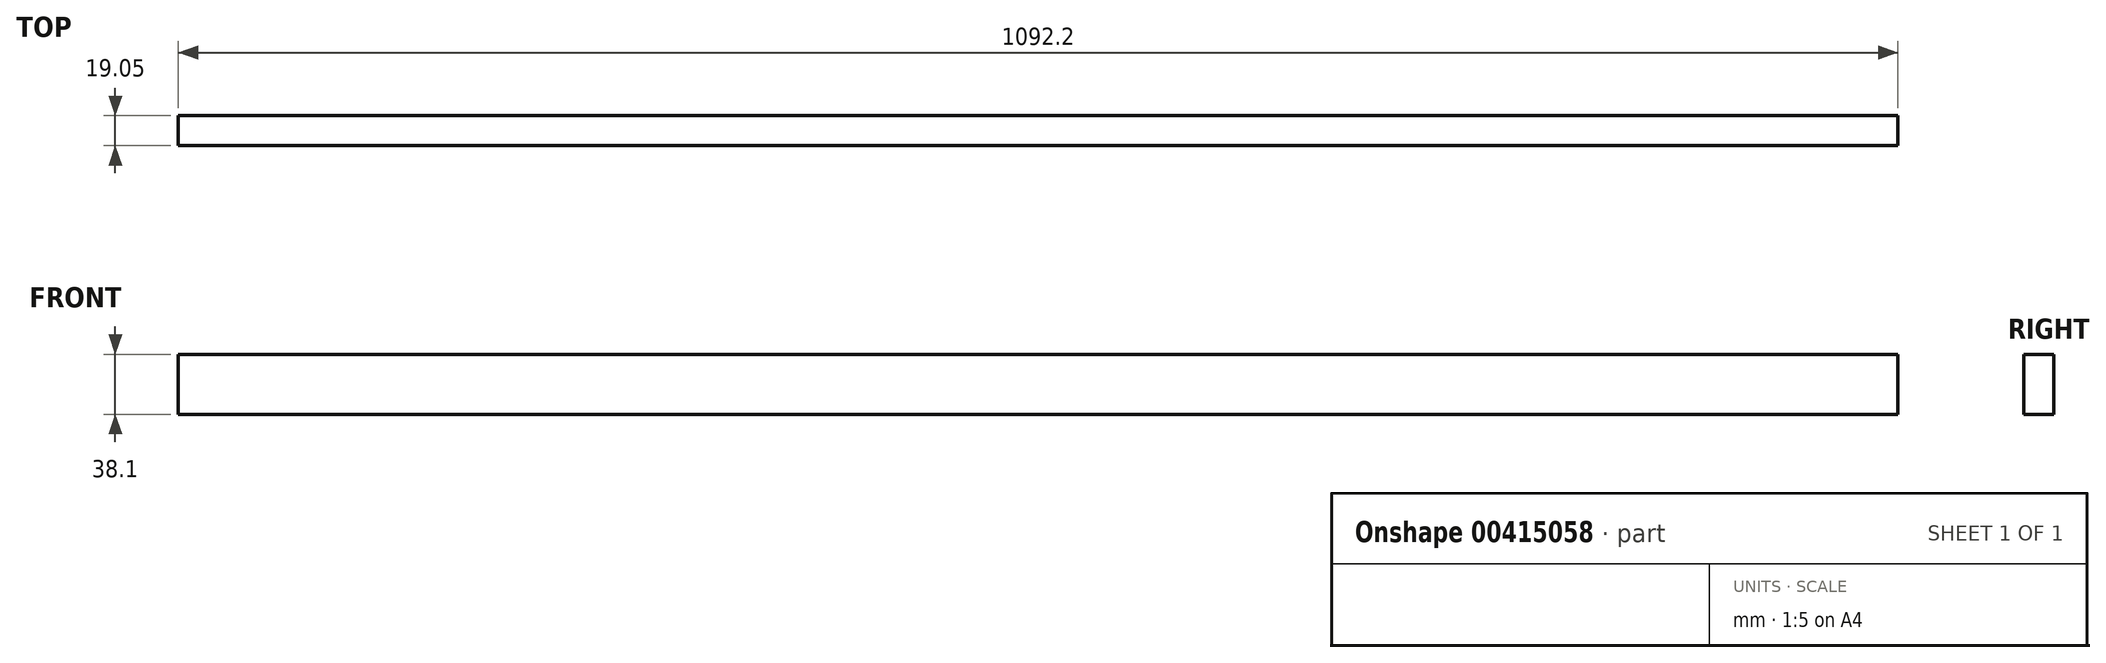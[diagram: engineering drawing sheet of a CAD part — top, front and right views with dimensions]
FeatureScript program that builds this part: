
annotation { "Feature Type Name" : "Feature", "Feature Type Description" : "" }
export const myFeature = defineFeature(function(context is Context, id is Id, definition is map)
    precondition{}
    {
        {
            var Q0;
            Q0=qCreatedBy(makeId("Front.planeOp"),FACE);
            var sketch = newSketch(context, id + "F0", { "sketchPlane" : qUnion([Q0])});
            skLineSegment(sketch, "E0.bottom", {"start": v(0, 0) * mm, "end": v(1092.2, 0) * mm});
            skLineSegment(sketch, "E0.top", {"start": v(0, 38.1) * mm, "end": v(1092.2, 38.1) * mm});
            skLineSegment(sketch, "E0.left", {"start": v(0, 0) * mm, "end": v(0, 38.1) * mm});
            skLineSegment(sketch, "E0.right", {"start": v(1092.2, 0) * mm, "end": v(1092.2, 38.1) * mm});
            skSolve(sketch);
        }
        {
            var Q0;
            Q0=makeQuery(id+"F0.imprint","IMPRINT",FACE,{"disambiguationData":[TD([[makeQuery(id+"F0.imprint","IMPRINT",EDGE,{"derivedFrom":sQuery(id+"F0.wireOp",EDGE,"E0.bottom")}),1.0]])]});
            extrude(context, id + "F1", {"entities" : qUnion([Q0]), "depth" : 19.05 * mm});
        }
    });
